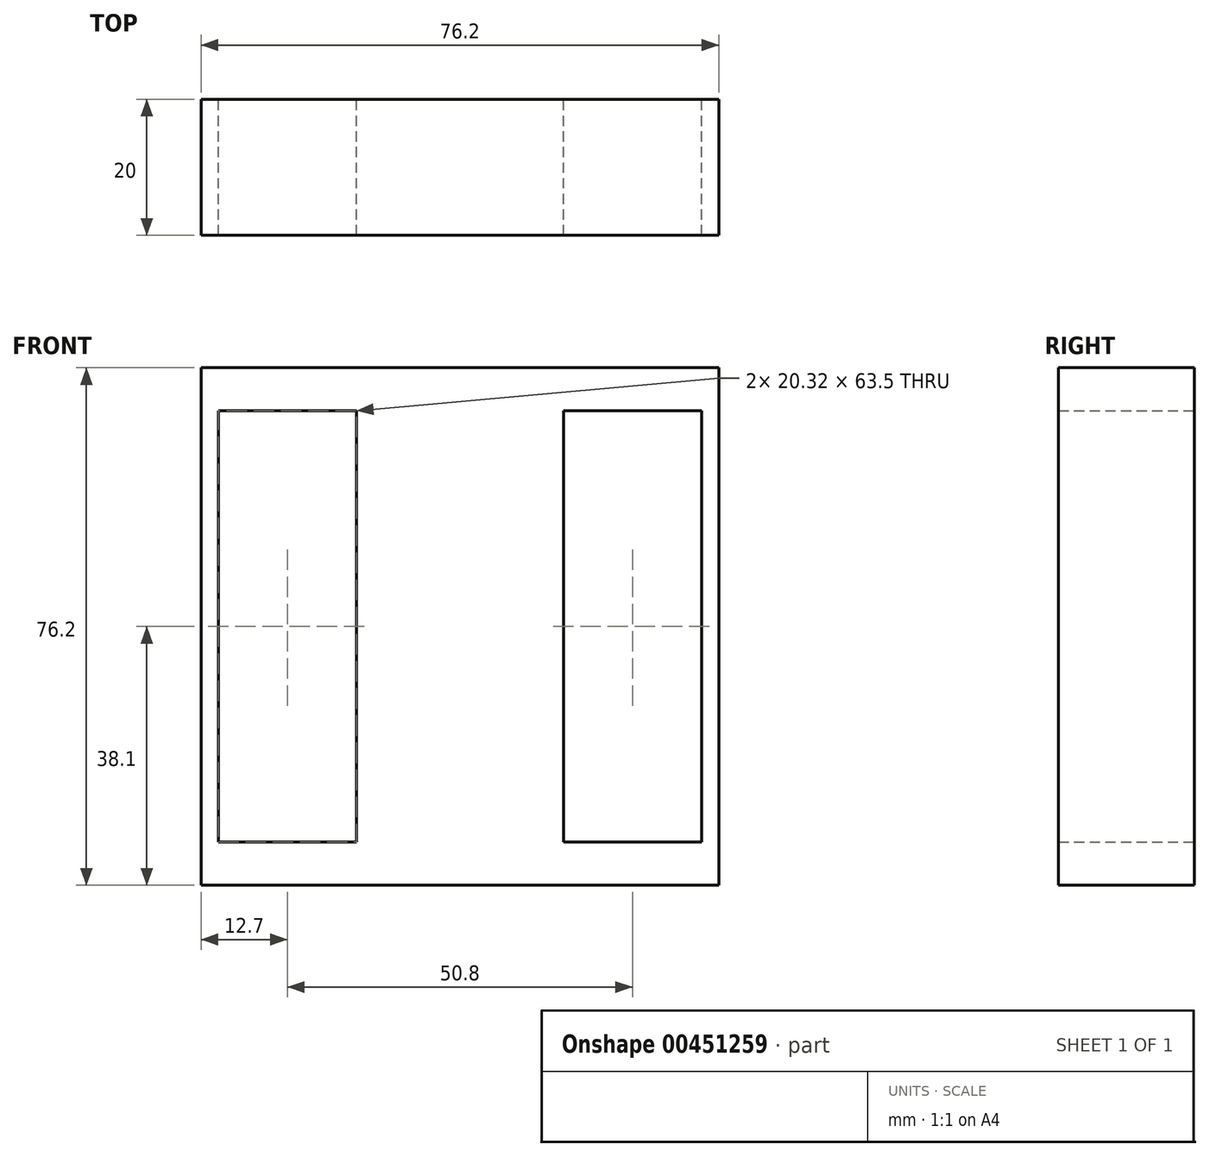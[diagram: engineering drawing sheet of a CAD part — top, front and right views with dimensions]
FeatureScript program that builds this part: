
annotation { "Feature Type Name" : "Feature", "Feature Type Description" : "" }
export const myFeature = defineFeature(function(context is Context, id is Id, definition is map)
    precondition{}
    {
        {
            var Q0;
            Q0=qCreatedBy(makeId("Front.planeOp"),FACE);
            var sketch = newSketch(context, id + "F0", { "sketchPlane" : qUnion([Q0])});
            skLineSegment(sketch, "E0.bottom", {"start": v(38.1, -38.1) * mm, "end": v(-38.1, -38.1) * mm});
            skLineSegment(sketch, "E0.top", {"start": v(38.1, 38.1) * mm, "end": v(-38.1, 38.1) * mm});
            skLineSegment(sketch, "E0.left", {"start": v(38.1, -38.1) * mm, "end": v(38.1, 38.1) * mm});
            skLineSegment(sketch, "E0.right", {"start": v(-38.1, -38.1) * mm, "end": v(-38.1, 38.1) * mm});
            skPoint(sketch, "E0.middle", {"position": v(0, 0) * mm});
            skLineSegment(sketch, "E1.bottom", {"start": v(-35.56, 31.75) * mm, "end": v(-15.24, 31.75) * mm});
            skLineSegment(sketch, "E1.top", {"start": v(-35.56, -31.75) * mm, "end": v(-15.24, -31.75) * mm});
            skLineSegment(sketch, "E1.left", {"start": v(-35.56, 31.75) * mm, "end": v(-35.56, -31.75) * mm});
            skLineSegment(sketch, "E1.right", {"start": v(-15.24, 31.75) * mm, "end": v(-15.24, -31.75) * mm});
            skLineSegment(sketch, "E2.bottom", {"start": v(15.24, 31.75) * mm, "end": v(35.56, 31.75) * mm});
            skLineSegment(sketch, "E2.top", {"start": v(15.24, -31.75) * mm, "end": v(35.56, -31.75) * mm});
            skLineSegment(sketch, "E2.left", {"start": v(15.24, 31.75) * mm, "end": v(15.24, -31.75) * mm});
            skLineSegment(sketch, "E2.right", {"start": v(35.56, 31.75) * mm, "end": v(35.56, -31.75) * mm});
            skSolve(sketch);
        }
        {
            var Q0;
            Q0 = qSketchRegion(id + "F0", true);
            extrude(context, id + "F1", {"entities" : qUnion([Q0]), "depth" : 20 * mm});
        }
    });
